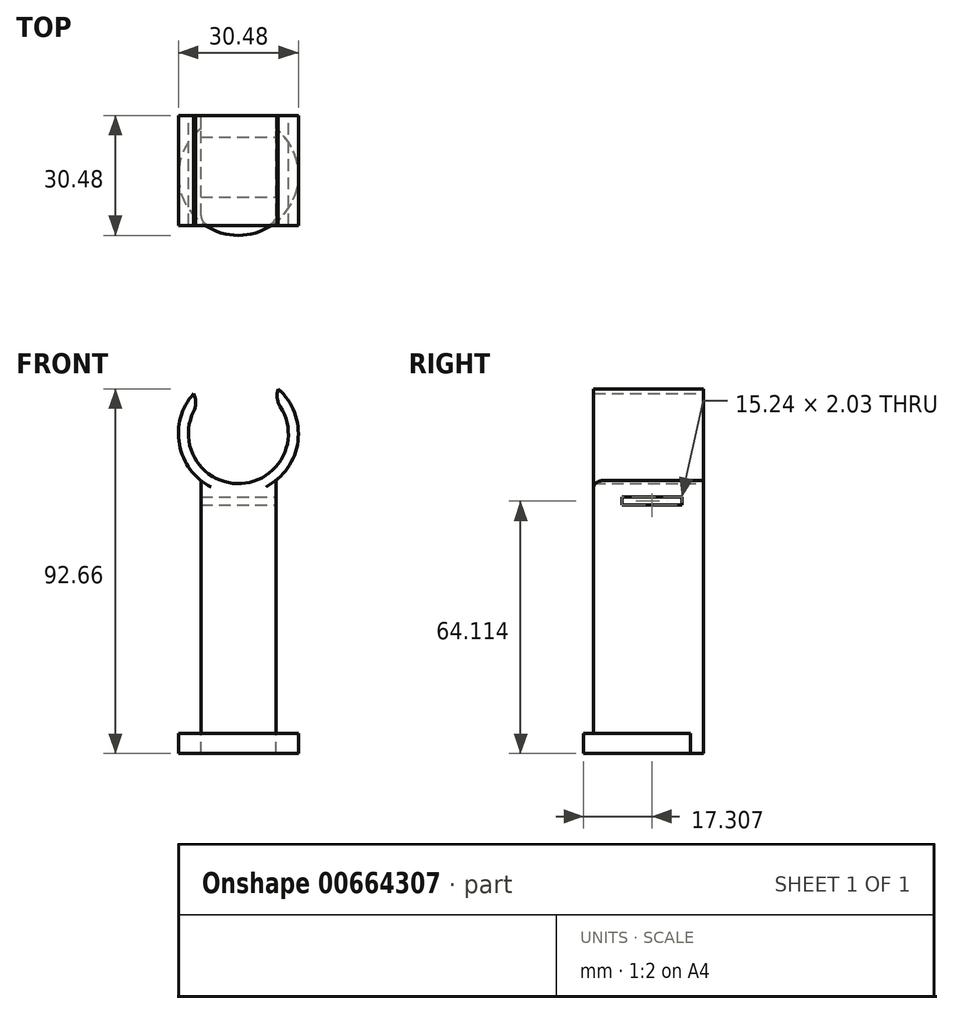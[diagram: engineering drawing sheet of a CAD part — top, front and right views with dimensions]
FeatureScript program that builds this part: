
annotation { "Feature Type Name" : "Feature", "Feature Type Description" : "" }
export const myFeature = defineFeature(function(context is Context, id is Id, definition is map)
    precondition{}
    {
        {
            var Q0;
            Q0=qCreatedBy(makeId("Front.planeOp"),FACE);
            var sketch = newSketch(context, id + "F0", { "sketchPlane" : qUnion([Q0])});
            skCircle(sketch, "E0", {"center": v(0, 0) * mm, "radius": 12.7 * mm});
            skCircle(sketch, "E1", {"center": v(0, 0) * mm, "radius": 15.24 * mm});
            skLineSegment(sketch, "E2", {"start": v(0, 0) * mm, "end": v(-16.77, 14.92) * mm});
            skLineSegment(sketch, "E3", {"start": v(0, 0) * mm, "end": v(12.99, 14.6) * mm});
            skLineSegment(sketch, "E4.bottom", {"start": v(-9.53, -11.9) * mm, "end": v(9.53, -11.9) * mm});
            skLineSegment(sketch, "E4.top", {"start": v(-9.53, -25.4) * mm, "end": v(9.53, -25.4) * mm});
            skLineSegment(sketch, "E4.left", {"start": v(-9.53, -11.9) * mm, "end": v(-9.53, -25.4) * mm});
            skLineSegment(sketch, "E4.right", {"start": v(9.53, -11.9) * mm, "end": v(9.53, -25.4) * mm});
            skSolve(sketch);
        }
        {
            var Q0;
            {var subQ0=sQuery(id+"F0.wireOp",EDGE,"E2");var subQ1=sQuery(id+"F0.wireOp",EDGE,"E0");var subQ2=makeQuery(id+"F0.imprint","INTERSECT",VERTEX,{"derivedFrom":[subQ1,subQ0]});Q0=makeQuery(id+"F0.imprint","IMPRINT",FACE,{"disambiguationData":[TD([[makeQuery(id+"F0.imprint","IMPRINT",EDGE,{"disambiguationData":[TD([[subQ2,-1.0]])],"derivedFrom":subQ1}),-1.0]])]});}
            var Q1;
            {var subQ0=sQuery(id+"F0.wireOp",EDGE,"E4.bottom");var subQ1=sQuery(id+"F0.wireOp",EDGE,"E0");var subQ2=makeQuery(id+"F0.imprint","INTERSECT",VERTEX,{"disambiguationData":[OD(0.0)],"derivedFrom":[subQ1,subQ0]});Q1=makeQuery(id+"F0.imprint","IMPRINT",FACE,{"disambiguationData":[TD([[makeQuery(id+"F0.imprint","IMPRINT",EDGE,{"disambiguationData":[TD([[subQ2,-1.0]])],"derivedFrom":subQ1}),-1.0]])]});}
            var Q2;
            Q2=makeQuery(id+"F0.imprint","IMPRINT",FACE,{"disambiguationData":[TD([[makeQuery(id+"F0.imprint","IMPRINT",EDGE,{"derivedFrom":sQuery(id+"F0.wireOp",EDGE,"E4.top")}),1.0]])]});
            var Q3;
            {var subQ0=sQuery(id+"F0.wireOp",EDGE,"E3");var subQ1=sQuery(id+"F0.wireOp",EDGE,"E0");var subQ2=makeQuery(id+"F0.imprint","INTERSECT",VERTEX,{"derivedFrom":[subQ1,subQ0]});Q3=makeQuery(id+"F0.imprint","IMPRINT",FACE,{"disambiguationData":[TD([[makeQuery(id+"F0.imprint","IMPRINT",EDGE,{"disambiguationData":[TD([[subQ2,1.0]])],"derivedFrom":subQ1}),-1.0]])]});}
            var Q4;
            {var subQ0=sQuery(id+"F0.wireOp",EDGE,"E4.bottom");var subQ1=sQuery(id+"F0.wireOp",EDGE,"E0");var subQ2=makeQuery(id+"F0.imprint","INTERSECT",VERTEX,{"disambiguationData":[OD(0.0)],"derivedFrom":[subQ1,subQ0]});Q4=makeQuery(id+"F0.imprint","IMPRINT",FACE,{"disambiguationData":[TD([[makeQuery(id+"F0.imprint","IMPRINT",EDGE,{"disambiguationData":[TD([[subQ2,1.0]])],"derivedFrom":subQ1}),-1.0]])]});}
            extrude(context, id + "F1", {"entities" : qUnion([Q0, Q1, Q2, Q3, Q4]), "depth" : 27.94 * mm, "offsetDistance" : 25.4 * mm});
        }
        {
            var Q0;
            Q0=makeQuery(id+"F1.opExtrude","SWEPT_FACE",FACE,{"disambiguationData":[OSD([sQuery(id+"F0.wireOp",EDGE,"E4.top")])]});
            var sketch = newSketch(context, id + "F2", { "sketchPlane" : qUnion([Q0])});
            skCircle(sketch, "E5", {"center": v(0, 13.97) * mm, "radius": 14.6 * mm});
            skSolve(sketch);
        }
        {
            var Q0;
            {var subQ0=sQuery(id+"F0.wireOp",EDGE,"E4.top");Q0=makeQuery(id+"F2.imprint","IMPRINT",FACE,{"disambiguationData":[TD([[makeQuery(id+"F2.imprint","IMPRINT",EDGE,{"derivedFrom":makeQuery(id+"F1.opExtrude","CAP_EDGE",EDGE,{"disambiguationData":[OSD([subQ0])],"isStart":true})}),1.0]])]});}
            var Q1;
            Q1=makeQuery(id+"F2.imprint","IMPRINT",FACE,{"disambiguationData":[TD([[makeQuery(id+"F2.imprint","IMPRINT",EDGE,{"derivedFrom":sQuery(id+"F2.wireOp",EDGE,"E5")}),1.0]])]});
            var Q2;
            {var subQ0=sQuery(id+"F2.wireOp",EDGE,"E5");var subQ1=sQuery(id+"F0.wireOp",EDGE,"E4.top");var subQ2=makeQuery(id+"F1.opExtrude","CAP_EDGE",EDGE,{"disambiguationData":[OSD([subQ1])],"isStart":false});var subQ3=makeQuery(id+"F2.imprint","INTERSECT",VERTEX,{"disambiguationData":[OD(1.0)],"derivedFrom":[subQ2,subQ0]});Q2=makeQuery(id+"F2.imprint","IMPRINT",FACE,{"disambiguationData":[TD([[makeQuery(id+"F2.imprint","IMPRINT",EDGE,{"disambiguationData":[TD([[subQ3,-1.0]])],"derivedFrom":subQ0}),-1.0]])]});}
            var Q3;
            {var subQ0=sQuery(id+"F2.wireOp",EDGE,"E5");var subQ1=sQuery(id+"F0.wireOp",EDGE,"E4.top");var subQ2=makeQuery(id+"F1.opExtrude","CAP_EDGE",EDGE,{"disambiguationData":[OSD([subQ1])],"isStart":false});var subQ3=makeQuery(id+"F2.imprint","INTERSECT",VERTEX,{"disambiguationData":[OD(0.0)],"derivedFrom":[subQ2,subQ0]});Q3=makeQuery(id+"F2.imprint","IMPRINT",FACE,{"disambiguationData":[TD([[makeQuery(id+"F2.imprint","IMPRINT",EDGE,{"disambiguationData":[TD([[subQ3,1.0]])],"derivedFrom":subQ0}),-1.0]])]});}
            var Q4;
            Q4=sQuery(id+"F2.wireOp",EDGE,"E5");
            extrude(context, id + "F3", {"entities" : qUnion([Q0, Q1, Q2, Q3]), "operationType" : NewBodyOperationType.ADD, "surfaceEntities" : qUnion([Q4]), "depth" : 50.8 * mm, "offsetDistance" : 25.4 * mm});
        }
        {
            var Q0;
            Q0=makeQuery(id+"F1.opExtrude","SWEPT_EDGE",EDGE,{"disambiguationData":[OSD([sQuery(id+"F0.wireOp",EDGE,"E0"),sQuery(id+"F0.wireOp",EDGE,"E2")])]});
            var Q1;
            Q1=makeQuery(id+"F1.opExtrude","SWEPT_EDGE",EDGE,{"disambiguationData":[OSD([sQuery(id+"F0.wireOp",EDGE,"E0"),sQuery(id+"F0.wireOp",EDGE,"E3")])]});
            fillet(context, id + "F4", {"entities" : qUnion([Q0, Q1]), "radius" : 5.08 * mm, "tangentPropagation" : true, "allowEdgeOverflow" : false});
        }
        {
            var Q0;
            Q0=makeQuery(id+"F1.opExtrude","CAP_EDGE",EDGE,{"disambiguationData":[OSD([sQuery(id+"F0.wireOp",EDGE,"E4.left")])],"isStart":false});
            var Q1;
            Q1=makeQuery(id+"F1.opExtrude","CAP_EDGE",EDGE,{"disambiguationData":[OSD([sQuery(id+"F0.wireOp",EDGE,"E4.right")])],"isStart":false});
            fillet(context, id + "F5", {"entities" : qUnion([Q0, Q1]), "radius" : 2.54 * mm, "tangentPropagation" : true, "allowEdgeOverflow" : false});
        }
        {
            var Q0;
            Q0=makeQuery(id+"F1.opExtrude","SWEPT_FACE",FACE,{"disambiguationData":[OSD([sQuery(id+"F0.wireOp",EDGE,"E4.right")])]});
            var sketch = newSketch(context, id + "F6", { "sketchPlane" : qUnion([Q0])});
            skLineSegment(sketch, "E6.bottom", {"start": v(-20.8, -16.15) * mm, "end": v(-5.55, -16.15) * mm});
            skLineSegment(sketch, "E6.top", {"start": v(-20.8, -18.18) * mm, "end": v(-5.55, -18.18) * mm});
            skLineSegment(sketch, "E6.left", {"start": v(-20.8, -16.15) * mm, "end": v(-20.8, -18.18) * mm});
            skLineSegment(sketch, "E6.right", {"start": v(-5.55, -16.15) * mm, "end": v(-5.55, -18.18) * mm});
            skSolve(sketch);
        }
        {
            var Q0;
            Q0=makeQuery(id+"F6.imprint","IMPRINT",FACE,{"disambiguationData":[TD([[makeQuery(id+"F6.imprint","IMPRINT",EDGE,{"derivedFrom":sQuery(id+"F6.wireOp",EDGE,"E6.bottom")}),-1.0]])]});
            extrude(context, id + "F7", {"entities" : qUnion([Q0]), "operationType" : NewBodyOperationType.REMOVE, "oppositeDirection" : true, "depth" : 25.4 * mm, "offsetDistance" : 25.4 * mm});
        }
        {
            var Q0;
            Q0=makeQuery(id+"F3.opExtrude","CAP_FACE",FACE,{"disambiguationData":[OSD([sQuery(id+"F0.wireOp",EDGE,"E4.top"),sQuery(id+"F0.wireOp",EDGE,"E4.left"),sQuery(id+"F0.wireOp",EDGE,"E4.right"),sQuery(id+"F2.wireOp",EDGE,"E5")])],"isStart":false});
            var sketch = newSketch(context, id + "F8", { "sketchPlane" : qUnion([Q0])});
            skCircle(sketch, "E7", {"center": v(0, 15.24) * mm, "radius": 15.24 * mm});
            skSolve(sketch);
        }
        {
            var Q0;
            {var subQ1=sQuery(id+"F2.wireOp",EDGE,"E5");var subQ2=sQuery(id+"F0.wireOp",EDGE,"E4.top");var subQ3=makeQuery(id+"F1.opExtrude","CAP_EDGE",EDGE,{"disambiguationData":[OSD([subQ2])],"isStart":false});var subQ4=makeQuery(id+"F3.opExtrude","CAP_EDGE",EDGE,{"disambiguationData":[OSD([subQ2]),TDD([makeQuery(id+"F2.imprint","IMPRINT",EDGE,{"disambiguationData":[TD([[makeQuery(id+"F2.imprint","INTERSECT",VERTEX,{"disambiguationData":[OD(0.0)],"derivedFrom":[subQ3,subQ1]}),1.0]])],"derivedFrom":subQ3})])],"isStart":false});Q0=makeQuery(id+"F8.imprint","IMPRINT",FACE,{"disambiguationData":[TD([[makeQuery(id+"F8.imprint","IMPRINT",EDGE,{"derivedFrom":subQ4}),1.0]])]});}
            var Q1;
            {var subQ0=sQuery(id+"F2.wireOp",EDGE,"E5");var subQ1=sQuery(id+"F0.wireOp",EDGE,"E4.top");var subQ2=makeQuery(id+"F1.opExtrude","CAP_EDGE",EDGE,{"disambiguationData":[OSD([subQ1])],"isStart":false});var subQ6=makeQuery(id+"F2.imprint","INTERSECT",VERTEX,{"disambiguationData":[OD(0.0)],"derivedFrom":[subQ2,subQ0]});Q1=makeQuery(id+"F8.imprint","IMPRINT",FACE,{"disambiguationData":[TD([[makeQuery(id+"F8.imprint","IMPRINT",EDGE,{"derivedFrom":makeQuery(id+"F3.opExtrude","CAP_EDGE",EDGE,{"disambiguationData":[OSD([subQ1]),TDD([makeQuery(id+"F2.imprint","IMPRINT",EDGE,{"disambiguationData":[TD([[subQ6,1.0]])],"derivedFrom":subQ2})])],"isStart":false})}),-1.0]])]});}
            extrude(context, id + "F9", {"entities" : qUnion([Q0, Q1]), "operationType" : NewBodyOperationType.ADD, "depth" : 5.08 * mm, "offsetDistance" : 25.4 * mm});
        }
        {
            var Q0;
            {var subQ0=sQuery(id+"F2.wireOp",EDGE,"E5");var subQ1=sQuery(id+"F0.wireOp",EDGE,"E4.top");var subQ3=sQuery(id+"F0.wireOp",EDGE,"E4.right");var subQ5=sQuery(id+"F0.wireOp",EDGE,"E4.left");Q0=makeQuery(id+"F9.boolean.opBoolean","SPLIT",FACE,{"disambiguationData":[TD([makeQuery(id+"F1.opExtrude","SWEPT_FACE",FACE,{"disambiguationData":[OSD([subQ5])]})])],"derivedFrom":makeQuery(id+"F3.opExtrude","CAP_FACE",FACE,{"disambiguationData":[OSD([subQ1,subQ5,subQ3,subQ0])],"isStart":false})});}
            var Q1;
            {var subQ0=sQuery(id+"F2.wireOp",EDGE,"E5");var subQ1=sQuery(id+"F0.wireOp",EDGE,"E4.top");var subQ3=sQuery(id+"F0.wireOp",EDGE,"E4.right");var subQ5=sQuery(id+"F0.wireOp",EDGE,"E4.left");Q1=makeQuery(id+"F9.boolean.opBoolean","SPLIT",FACE,{"disambiguationData":[TD([makeQuery(id+"F1.opExtrude","SWEPT_FACE",FACE,{"disambiguationData":[OSD([subQ3])]})])],"derivedFrom":makeQuery(id+"F3.opExtrude","CAP_FACE",FACE,{"disambiguationData":[OSD([subQ1,subQ5,subQ3,subQ0])],"isStart":false})});}
            extrude(context, id + "F10", {"entities" : qUnion([Q0, Q1]), "operationType" : NewBodyOperationType.ADD, "depth" : 5.08 * mm, "offsetDistance" : 25.4 * mm});
        }
    });
